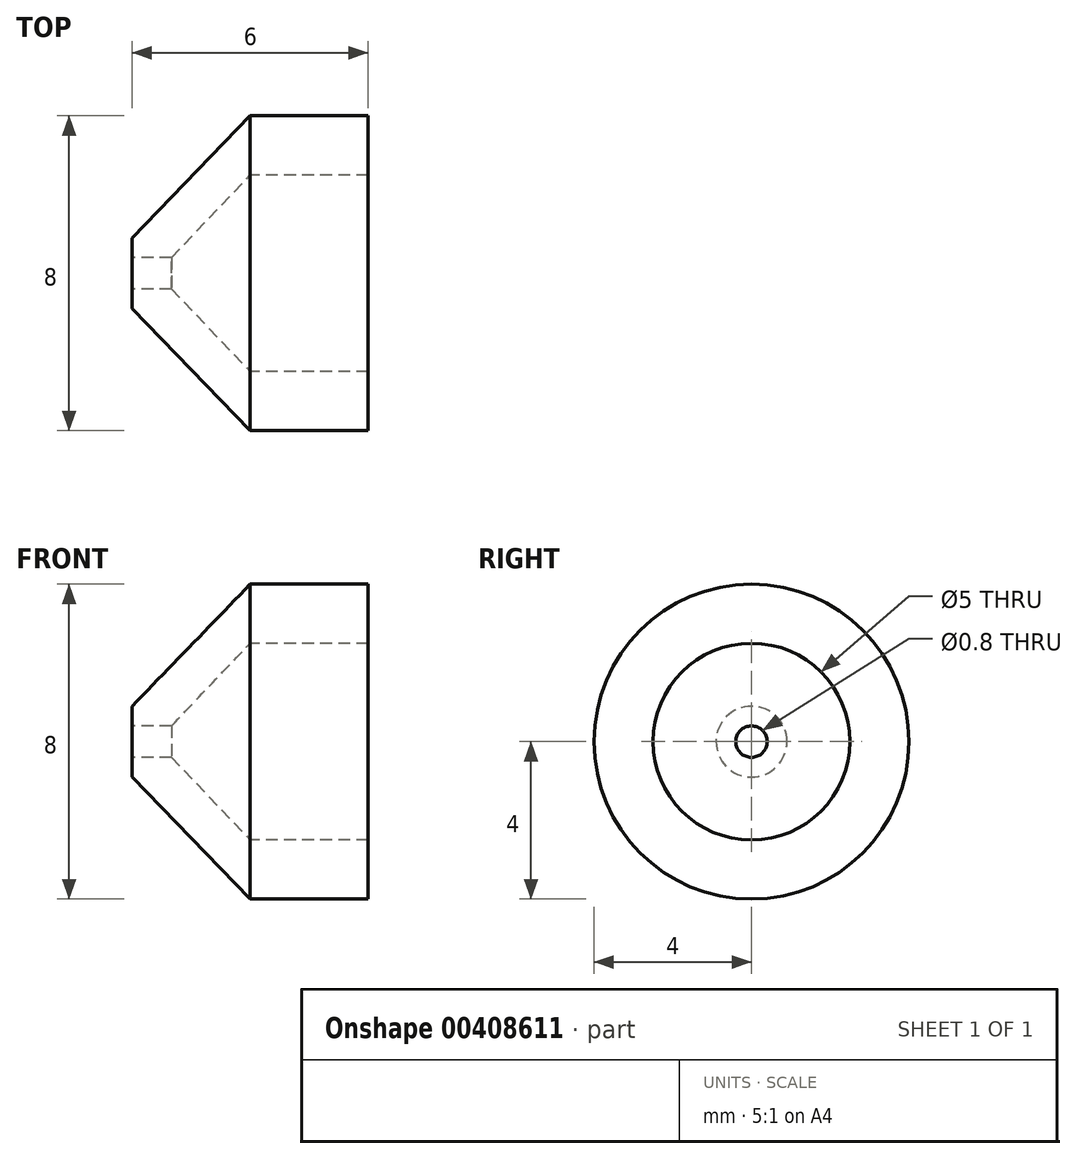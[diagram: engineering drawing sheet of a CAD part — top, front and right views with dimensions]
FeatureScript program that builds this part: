
annotation { "Feature Type Name" : "Feature", "Feature Type Description" : "" }
export const myFeature = defineFeature(function(context is Context, id is Id, definition is map)
    precondition{}
    {
        {
            var Q0;
            Q0=qCreatedBy(makeId("Top.planeOp"),FACE);
            var sketch = newSketch(context, id + "F0", { "sketchPlane" : qUnion([Q0])});
            skLineSegment(sketch, "E0", {"start": v(0, 2.5) * mm, "end": v(-3, 2.5) * mm});
            skLineSegment(sketch, "E1", {"start": v(-3, 2.5) * mm, "end": v(-5, 0.4) * mm});
            skLineSegment(sketch, "E2", {"start": v(-5, 0.4) * mm, "end": v(-6, 0.4) * mm});
            skLineSegment(sketch, "E3", {"start": v(-6, 0.9) * mm, "end": v(-6, 0.4) * mm});
            skLineSegment(sketch, "E4", {"start": v(-6, 0.9) * mm, "end": v(-3, 4) * mm});
            skLineSegment(sketch, "E5", {"start": v(-3, 4) * mm, "end": v(0, 4) * mm});
            skLineSegment(sketch, "E6", {"start": v(0, 4) * mm, "end": v(0, 2.5) * mm});
            skLineSegment(sketch, "E7", {"start": v(-6, 0) * mm, "end": v(0, 0) * mm, "construction": true});
            skSolve(sketch);
        }
        {
            var Q0;
            Q0 = qSketchRegion(id + "F0", true);
            var Q1;
            Q1=sQuery(id+"F0.wireOp",EDGE,"E7");
            revolve(context, id + "F1", {"entities" : qUnion([Q0]), "axis" : qUnion([Q1]), "revolveType" : RevolveType.FULL});
        }
    });
